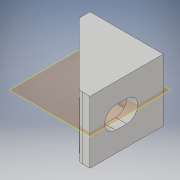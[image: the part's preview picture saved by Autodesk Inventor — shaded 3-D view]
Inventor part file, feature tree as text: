
AUTODESK INVENTOR PART (.ipt)
format: ipt  version: 2018 (Build 220112000, 112)  size: 150,016 bytes
history: native  units: in
note: dims shown in document units (in); Inventor stores cm internally (conversion verified against a paired STEP export)
features: extrude x4, sketch x4, mirror x1, fillet x1
ambient origin geometry x8: Origin, YZ Plane, XZ Plane, XY Plane, X Axis, Y Axis, Z Axis, Center Point
bodies: Solid1 (feature_tree)
feature tree (10):
  extrude  "Extrusion1"  Depth=0.7874in
  extrude  "Extrusion2"  Depth=0.1181in
  extrude  "Extrusion3"  Depth=0.2362in
  extrude  "Extrusion4"  Depth=0.7874in TaperAngle=0.0deg
  mirror  "Mirror1"
  fillet  "Fillet1"  Radius=0.2362in
  sketch  "Sketch1"  dims[d0=0.7874in d1=0.7874in]
  sketch  "Sketch2"  dims[d2=0.1181in d3=0.1181in]
  sketch  "Sketch3"  dims[d4=0.6693in d5=0.0in d6=0.2362in]
  sketch  "Sketch4"  dims[d7=0.1181in d8=0.7874in d9=0.0in d10=0.2362in d11=0.1181in d12=0.7874in d13=0.0in d14=0.0787in d15=0.0in d16=0.0787in]
